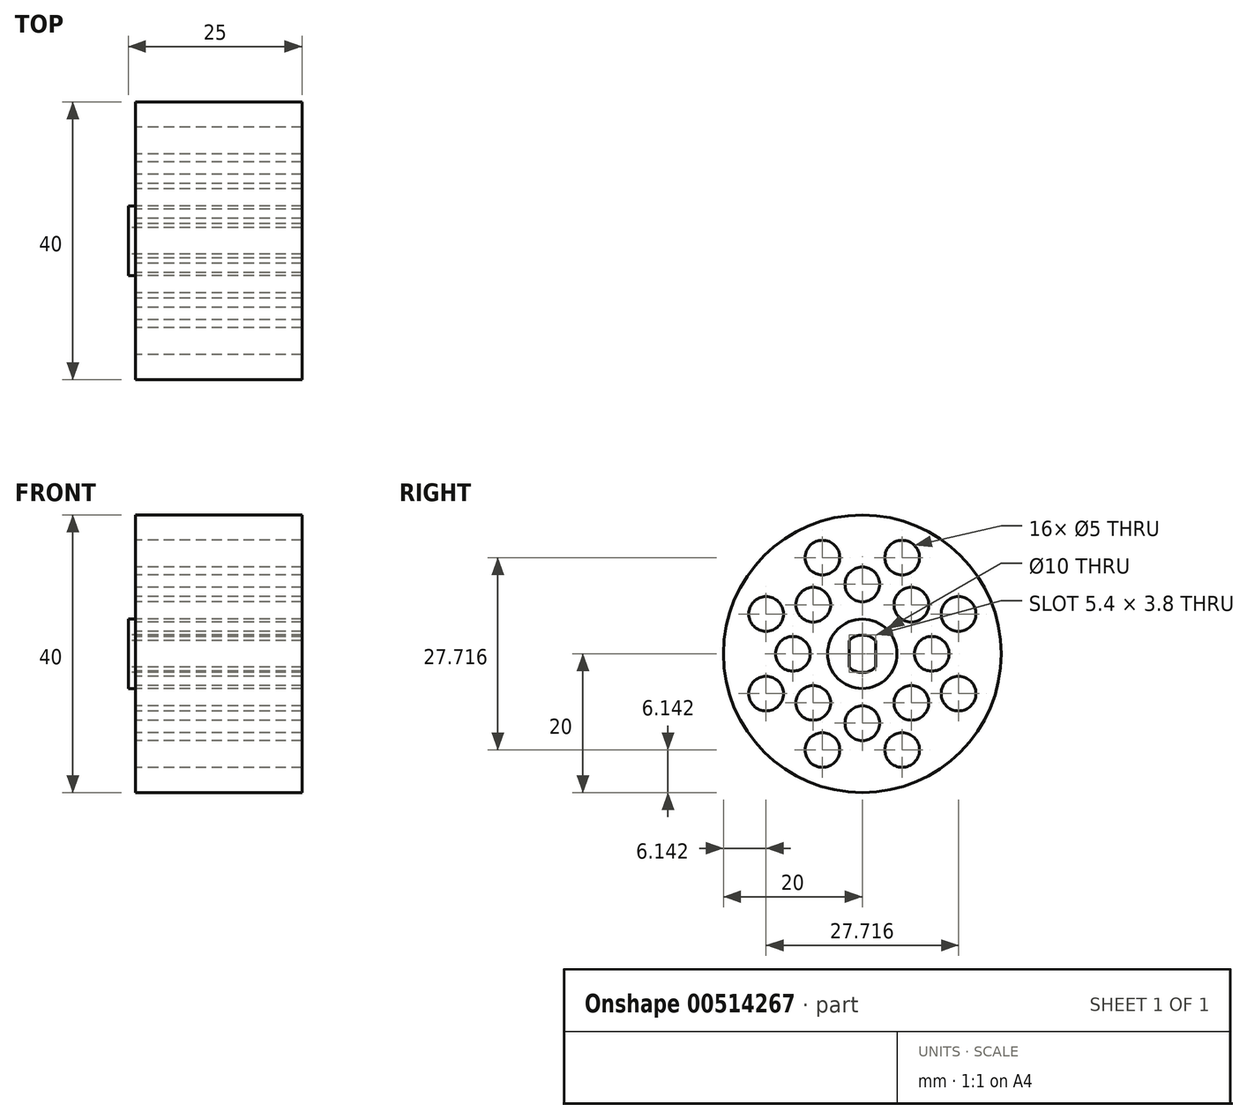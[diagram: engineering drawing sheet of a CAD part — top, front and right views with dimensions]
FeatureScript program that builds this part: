
annotation { "Feature Type Name" : "Feature", "Feature Type Description" : "" }
export const myFeature = defineFeature(function(context is Context, id is Id, definition is map)
    precondition{}
    {
        {
            var Q0;
            Q0=qCreatedBy(makeId("Right.planeOp"),FACE);
            var sketch = newSketch(context, id + "F0", { "sketchPlane" : qUnion([Q0])});
            skCircle(sketch, "E0", {"center": v(0, 0) * mm, "radius": 5 * mm});
            skArc(sketch, "E1", {"start": v(-1.9, -1.92) * mm, "mid": v(0, -2.7) * mm, "end": v(1.9, -1.92) * mm});
            skLineSegment(sketch, "E2.left", {"start": v(1.9, 1.92) * mm, "end": v(1.9, -1.92) * mm});
            skLineSegment(sketch, "E2.right", {"start": v(-1.9, 1.92) * mm, "end": v(-1.9, -1.92) * mm});
            skArc(sketch, "E3.trimOffspring", {"start": v(1.9, 1.92) * mm, "mid": v(0, 2.7) * mm, "end": v(-1.9, 1.92) * mm});
            skCircle(sketch, "E4.0", {"center": v(0, 0) * mm, "radius": 20 * mm});
            skCircle(sketch, "E5", {"center": v(0, 0) * mm, "radius": 10 * mm, "construction": true});
            skCircle(sketch, "E6", {"center": v(10, 0) * mm, "radius": 2.5 * mm});
            skCircle(sketch, "E7.1.0", {"center": v(7.07, 7.07) * mm, "radius": 2.5 * mm});
            skCircle(sketch, "E7.2.0", {"center": v(0, 10) * mm, "radius": 2.5 * mm});
            skCircle(sketch, "E7.3.0", {"center": v(-7.07, 7.07) * mm, "radius": 2.5 * mm});
            skCircle(sketch, "E7.4.0", {"center": v(-10, 0) * mm, "radius": 2.5 * mm});
            skCircle(sketch, "E7.5.0", {"center": v(-7.07, -7.07) * mm, "radius": 2.5 * mm});
            skCircle(sketch, "E7.6.0", {"center": v(0, -10) * mm, "radius": 2.5 * mm});
            skCircle(sketch, "E7.7.0", {"center": v(7.07, -7.07) * mm, "radius": 2.5 * mm});
            skCircle(sketch, "E8", {"center": v(0, 0) * mm, "radius": 15 * mm, "construction": true});
            skCircle(sketch, "E9", {"center": v(5.74, 13.86) * mm, "radius": 2.5 * mm});
            skLineSegment(sketch, "E10", {"start": v(0, 0) * mm, "end": v(5.74, 13.86) * mm, "construction": true});
            skCircle(sketch, "E11.1.0", {"center": v(-5.74, 13.86) * mm, "radius": 2.5 * mm});
            skCircle(sketch, "E11.2.0", {"center": v(-13.86, 5.74) * mm, "radius": 2.5 * mm});
            skCircle(sketch, "E11.3.0", {"center": v(-13.86, -5.74) * mm, "radius": 2.5 * mm});
            skCircle(sketch, "E11.4.0", {"center": v(-5.74, -13.86) * mm, "radius": 2.5 * mm});
            skCircle(sketch, "E11.5.0", {"center": v(5.74, -13.86) * mm, "radius": 2.5 * mm});
            skCircle(sketch, "E11.6.0", {"center": v(13.86, -5.74) * mm, "radius": 2.5 * mm});
            skCircle(sketch, "E11.7.0", {"center": v(13.86, 5.74) * mm, "radius": 2.5 * mm});
            skSolve(sketch);
        }
        {
            var Q0;
            Q0=makeQuery(id+"F0.imprint","IMPRINT",FACE,{"disambiguationData":[TD([[makeQuery(id+"F0.imprint","IMPRINT",EDGE,{"derivedFrom":sQuery(id+"F0.wireOp",EDGE,"E0")}),1.0]])]});
            extrude(context, id + "F1", {"entities" : qUnion([Q0]), "depth" : 25 * mm});
        }
        {
            var Q0;
            Q0=qSketchRegion(id+"F0",true);
            extrude(context, id + "F2", {"entities" : qUnion([Q0]), "depth" : 25 * mm, "hasSecondDirection" : true, "secondDirectionOppositeDirection" : true, "secondDirectionDepth" : -1 * mm});
        }
    });
